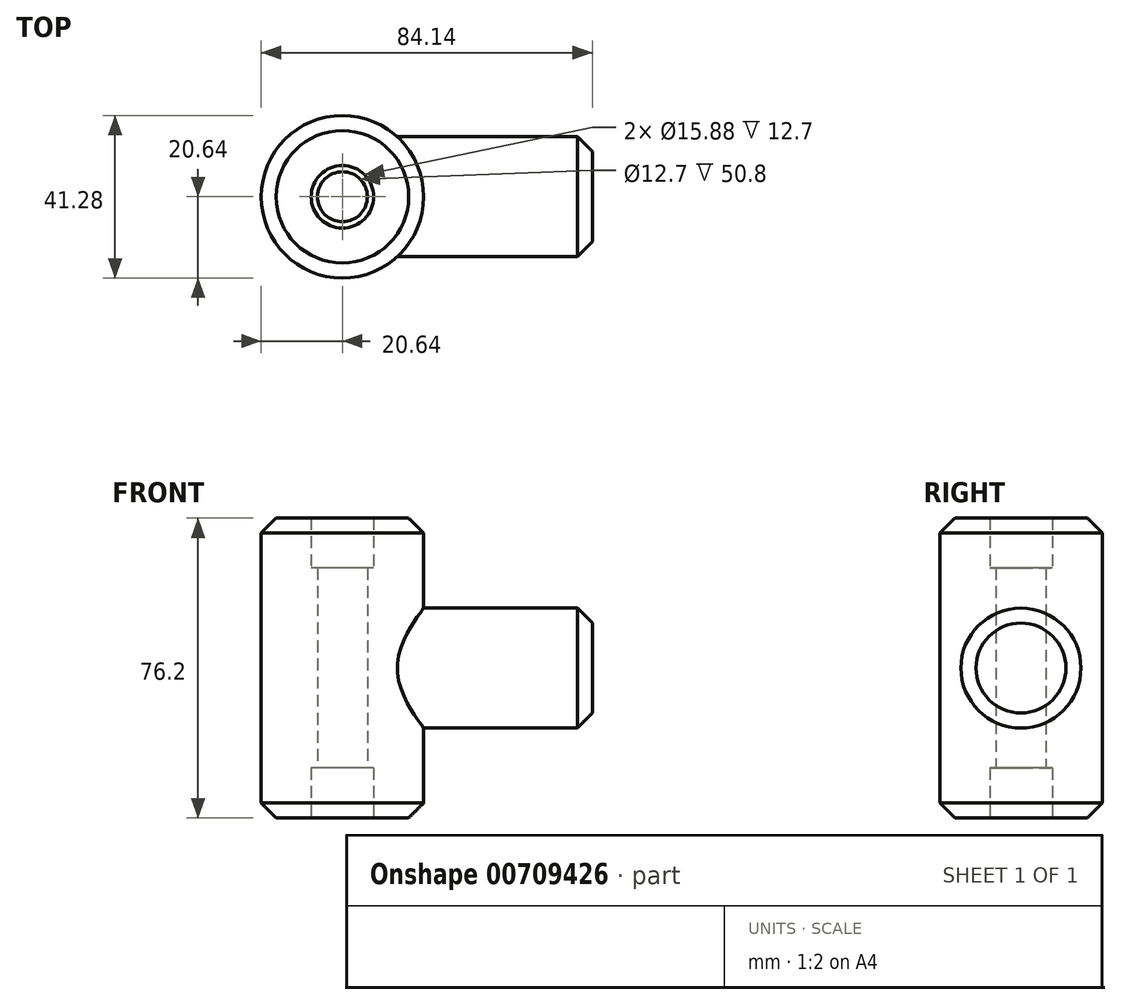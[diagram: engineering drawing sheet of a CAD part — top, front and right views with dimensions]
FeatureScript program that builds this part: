
annotation { "Feature Type Name" : "Feature", "Feature Type Description" : "" }
export const myFeature = defineFeature(function(context is Context, id is Id, definition is map)
    precondition{}
    {
        {
            var Q0;
            Q0=qCreatedBy(makeId("Top.planeOp"),FACE);
            var sketch = newSketch(context, id + "F0", { "sketchPlane" : qUnion([Q0])});
            skLineSegment(sketch, "E0", {"start": v(0, 0) * mm, "end": v(6.35, 0) * mm});
            skCircle(sketch, "E1", {"center": v(0, 0) * mm, "radius": 6.35 * mm});
            skCircle(sketch, "E2.0", {"center": v(0, 0) * mm, "radius": 7.94 * mm});
            skSolve(sketch);
        }
        {
            var Q0;
            Q0=makeQuery(id+"F0.imprint","IMPRINT",FACE,{"disambiguationData":[TD([[makeQuery(id+"F0.imprint","IMPRINT",EDGE,{"derivedFrom":sQuery(id+"F0.wireOp",EDGE,"E1")}),-1.0]])]});
            extrude(context, id + "F1", {"entities" : qUnion([Q0]), "depth" : 50.8 * mm, "offsetDistance" : 25.4 * mm});
        }
        {
            var Q0;
            Q0=qSketchRegion(id+"F0",true);
            var sketch = newSketch(context, id + "F2", { "sketchPlane" : qUnion([Q0])});
            skCircle(sketch, "E3.0", {"center": v(0, 0) * mm, "radius": 20.64 * mm});
            skSolve(sketch);
        }
        {
            var Q0;
            Q0=makeQuery(id+"F2.imprint","IMPRINT",FACE,{"disambiguationData":[TD([[makeQuery(id+"F2.imprint","IMPRINT",EDGE,{"derivedFrom":sQuery(id+"F2.wireOp",EDGE,"E3.0")}),1.0]])]});
            var Q1;
            Q1=sQuery(id+"F0.wireOp",EDGE,"E2.0");
            var Q2;
            Q2=sQuery(id+"F2.wireOp",EDGE,"E3.0");
            extrude(context, id + "F3", {"entities" : qUnion([Q0]), "operationType" : NewBodyOperationType.ADD, "surfaceEntities" : qUnion([Q1, Q2]), "depth" : 63.5 * mm, "offsetDistance" : 25.4 * mm, "hasSecondDirection" : true, "secondDirectionOppositeDirection" : true, "secondDirectionDepth" : 12.7 * mm});
        }
        {
            var Q0;
            Q0=qCreatedBy(makeId("Right.planeOp"),FACE);
            var sketch = newSketch(context, id + "F4", { "sketchPlane" : qUnion([Q0])});
            skCircle(sketch, "E4", {"center": v(0, 25.4) * mm, "radius": 15.24 * mm});
            skSolve(sketch);
        }
        {
            var Q0;
            Q0=qSketchRegion(id+"F4",true);
            extrude(context, id + "F5", {"entities" : qUnion([Q0]), "operationType" : NewBodyOperationType.ADD, "depth" : 63.5 * mm, "offsetDistance" : 25.4 * mm, "hasSecondDirection" : true, "secondDirectionOppositeDirection" : false, "secondDirectionDepth" : 12.7 * mm});
        }
        {
            var Q0;
            Q0=makeQuery(id+"F5.opExtrude","CAP_EDGE",EDGE,{"disambiguationData":[OSD([sQuery(id+"F4.wireOp",EDGE,"E4")])],"isStart":false});
            var Q1;
            Q1=makeQuery(id+"F3.opExtrude","CAP_EDGE",EDGE,{"disambiguationData":[OSD([sQuery(id+"F2.wireOp",EDGE,"E3.0")])],"isStart":false});
            chamfer(context, id + "F6", {"entities" : qUnion([Q0, Q1]), "width" : 3.8 * mm, "tangentPropagation" : true});
        }
        {
            var Q0;
            Q0=makeQuery(id+"F3.opExtrude","CAP_EDGE",EDGE,{"disambiguationData":[OSD([sQuery(id+"F2.wireOp",EDGE,"E3.0")])],"isStart":true});
            chamfer(context, id + "F7", {"entities" : qUnion([Q0]), "width" : 3.8 * mm, "tangentPropagation" : true});
        }
    });
